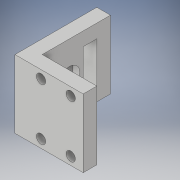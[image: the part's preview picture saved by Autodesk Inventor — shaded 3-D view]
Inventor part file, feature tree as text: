
AUTODESK INVENTOR PART (.ipt)
format: ipt  version: 2017 (Build 210142000, 142)  size: 154,624 bytes
history: native  units: in
note: dims shown in document units (in); Inventor stores cm internally (conversion verified against a paired STEP export)
features: extrude x3, sketch x3, projected_geometry x2
ambient origin geometry x8: Origin, YZ Plane, XZ Plane, XY Plane, X Axis, Y Axis, Z Axis, Center Point
bodies: Body1 (feature_tree)
feature tree (8):
  extrude  "Extrusion3"  Depth=1.5in
  extrude  "Extrusion4"  Depth=0.25in
  extrude  "Extrusion5"  Depth=0.25in
  sketch  "Sketch4"  dims[d36=1.25in d37=1.5in]
  sketch  "Sketch5"  dims[d38=0.75in d39=0.25in]
  projected_geometry  "Projected Loop2"
  sketch  "Sketch6"  dims[d40=0.25in d41=0.25in d42=0.25in d43=0.25in d44=0.25in d45=0.25in d46=0.0in d47=0.375in d48=0.125in d49=0.0in d50=1.25in d51=0.17in d53=0.147in d54=0.228in d55=0.17in d56=0.17in d57=0.17in d58=0.544in d59=0.147in d60=0.544in d61=0.228in d62=0.25in d63=0.0in d64=0.147in]
  projected_geometry  "Projected Loop3"
